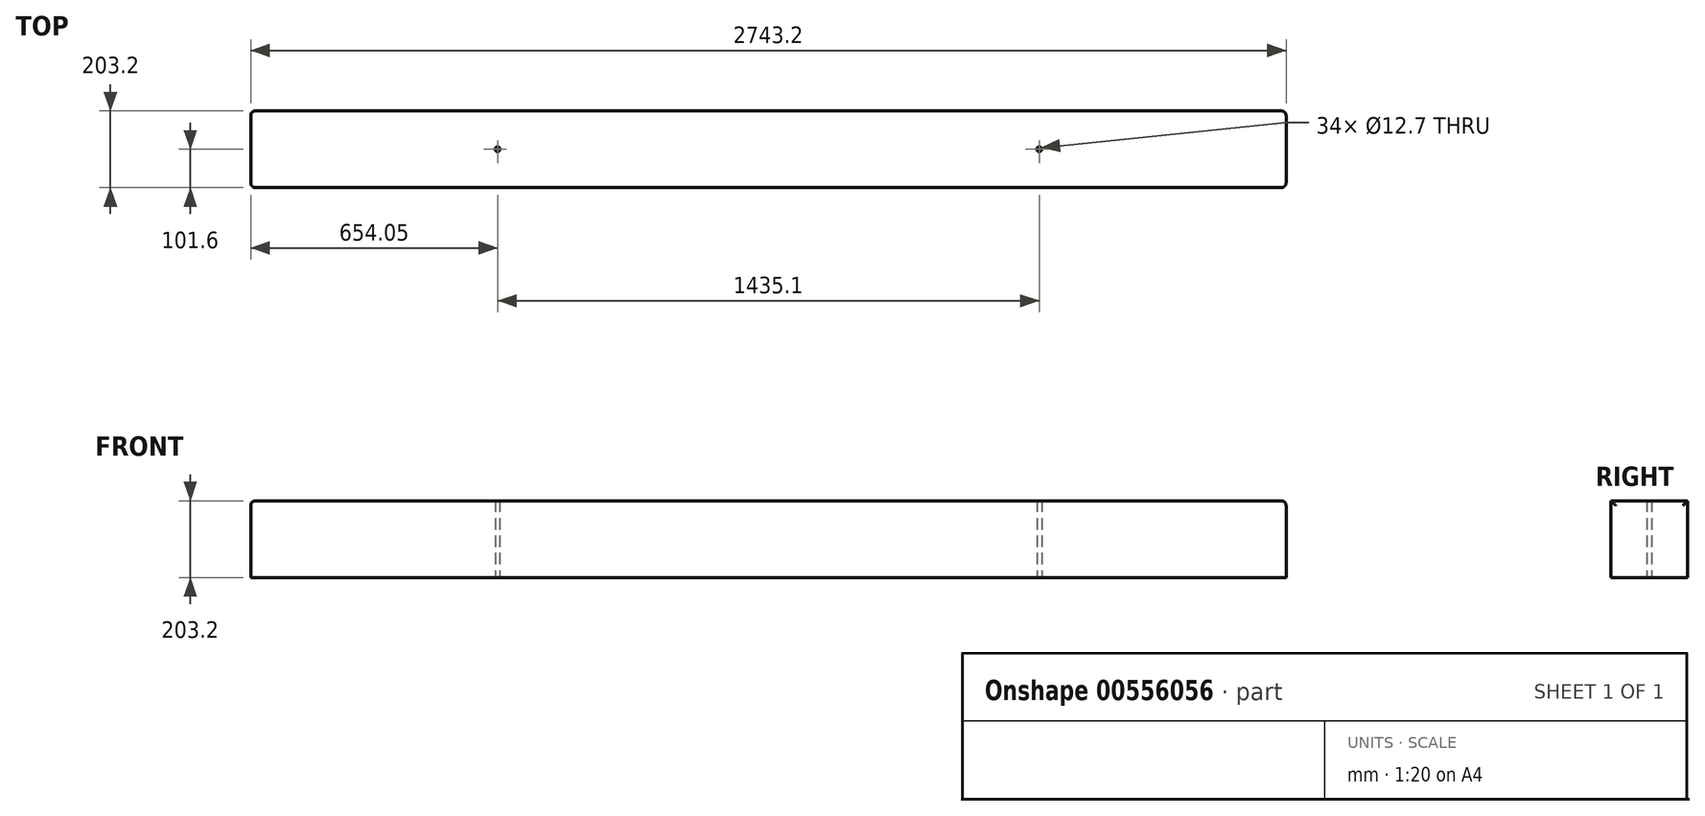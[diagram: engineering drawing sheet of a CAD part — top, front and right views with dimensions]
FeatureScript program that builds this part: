
annotation { "Feature Type Name" : "Feature", "Feature Type Description" : "" }
export const myFeature = defineFeature(function(context is Context, id is Id, definition is map)
    precondition{}
    {
        {
            var Q0;
            Q0=qCreatedBy(makeId("Top.planeOp"),FACE);
            var sketch = newSketch(context, id + "F0", { "sketchPlane" : qUnion([Q0])});
            skLineSegment(sketch, "E0", {"start": v(0, 0) * mm, "end": v(685.8, 0) * mm});
            skLineSegment(sketch, "E1", {"start": v(685.8, 0) * mm, "end": v(685.8, -203.2) * mm});
            skLineSegment(sketch, "E2", {"start": v(685.8, -203.2) * mm, "end": v(-2057.4, -203.2) * mm});
            skLineSegment(sketch, "E3", {"start": v(-2057.4, -203.2) * mm, "end": v(-2057.4, 0) * mm});
            skLineSegment(sketch, "E4", {"start": v(-2057.4, 0) * mm, "end": v(0, 0) * mm});
            skLineSegment(sketch, "E5", {"start": v(-685.8, -203.2) * mm, "end": v(-685.8, 0) * mm});
            skLineSegment(sketch, "E6", {"start": v(-685.8, -101.6) * mm, "end": v(-1403.35, -101.6) * mm});
            skLineSegment(sketch, "E7.MirrorCS", {"start": v(-685.8, -101.6) * mm, "end": v(31.75, -101.6) * mm});
            skCircle(sketch, "E8", {"center": v(-1403.35, -101.6) * mm, "radius": 6.35 * mm});
            skCircle(sketch, "E9.MirrorC", {"center": v(31.75, -101.6) * mm, "radius": 6.35 * mm});
            skSolve(sketch);
        }
        {
            var Q0;
            Q0 = qSketchRegion(id + "F0", true);
            extrude(context, id + "F1", {"entities" : qUnion([Q0]), "depth" : 203.2 * mm, "offsetDistance" : 25.4 * mm});
        }
        {
            var Q0;
            Q0=makeQuery(id+"F1.opExtrude","CAP_EDGE",EDGE,{"disambiguationData":[OSD([sQuery(id+"F0.wireOp",EDGE,"E1")])],"isStart":false});
            var Q1;
            Q1=makeQuery(id+"F1.opExtrude","SWEPT_EDGE",EDGE,{"disambiguationData":[OSD([sQuery(id+"F0.wireOp",EDGE,"E1"),sQuery(id+"F0.wireOp",EDGE,"E2")])]});
            var Q2;
            Q2=makeQuery(id+"F1.opExtrude","SWEPT_EDGE",EDGE,{"disambiguationData":[OSD([sQuery(id+"F0.wireOp",EDGE,"E0"),sQuery(id+"F0.wireOp",EDGE,"E1")])]});
            var Q3;
            Q3=makeQuery(id+"F1.opExtrude","SWEPT_EDGE",EDGE,{"disambiguationData":[OSD([sQuery(id+"F0.wireOp",EDGE,"E2"),sQuery(id+"F0.wireOp",EDGE,"E3")])]});
            var Q4;
            Q4=makeQuery(id+"F1.opExtrude","CAP_EDGE",EDGE,{"disambiguationData":[OSD([sQuery(id+"F0.wireOp",EDGE,"E3")])],"isStart":false});
            var Q5;
            Q5=makeQuery(id+"F1.opExtrude","SWEPT_EDGE",EDGE,{"disambiguationData":[OSD([sQuery(id+"F0.wireOp",EDGE,"E3"),sQuery(id+"F0.wireOp",EDGE,"E4")])]});
            fillet(context, id + "F2", {"entities" : qUnion([Q0, Q1, Q2, Q3, Q4, Q5]), "radius" : 12.7 * mm, "tangentPropagation" : true, "allowEdgeOverflow" : false});
        }
    });
